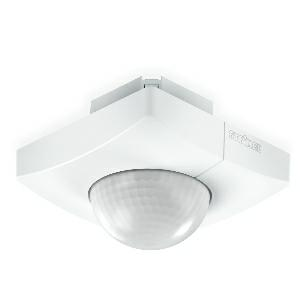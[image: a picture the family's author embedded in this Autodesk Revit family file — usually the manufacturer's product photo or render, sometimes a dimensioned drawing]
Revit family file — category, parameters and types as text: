
# Revit family: is_3360_033514
name_source: partatom
category: Elektroinstallationen
revit_build: Autodesk Revit 2016 (Build: 20190508_0715(x64)
units: mm (PartAtom-declared; Revit-internal decimal feet)

## family parameters
Basisbauteil = Fläche
Beim Laden mit Abzugskörper schneiden = Nein
Bemaßung runder Anschluss = Durchmesser verwenden
Beschriftungsausrichtung beibehalten = Nein
Gemeinsam genutzt = Nein
Raumberechnungspunkt = Nein
Teiletyp = Normal

## types (1)
- IS 3360
    Apparent Load = 0 VA
    Beschreibung = Type: Motion detectors; Dimensions (L x W x H): 78 x 94 x 94 mm; Mains power supply: 220 – 240 V / 50 – 60 Hz; Sensor Technology: passive infrared; Application, place: Indoors; Application, room: production facilities, recreation room, changing room, function room / ancillary room, sports hall, reception / lobby, stairwell, WC / washroom, multi-storey / underground car park, warehouse, Indoors; Installation site: ceiling; Installation: Concealed wiring; Switching zones: 1416 switching zones; Electronic scalability: No; Mechanical scalability: No; Mounting height: 2,50 – 4,00 m; Optimum mounting height: 2,8 m; Detection angle: 360 °; Angle of aperture: 180 °; Sneak-by guard: Yes; Capability of masking out individual segments: Yes; Reach, radial: Ø 8 m (50 m²); Reach, tangential: Ø 40 m (1257 m²); Reach, presence: Ø 3 m (7 m²); Twilight setting TEACH: Yes; Twilight setting: 2 – 1000 lx; Time setting: 5 sec – 15 min; Control output, Dali: Broadcast 1x30 electronic ballasts; Constant-lighting control: Yes; Basic light level function: Yes; Basic light level function in per cent: 10 – 50 %; Basic light level function time: 1-30 min, all night; Basic light level function percentage, from: 10 %; Basic light level function percentage, up to: 50 %; Functions: Normal / test mode, Manual ON / ON-OFF, Constant-lighting control ON-OFF; Settings via: Remote control, Potentiometers, Smart Remote; With remote control: No; Interconnection: Yes; IP-rating: IP20; Material: Plastic; Ambient temperature: -20 – 50 °C; Colour: white; Colour, RAL: 9003; Manufacturer's Warranty: 5 years; Version: DALI-2 Application Controller - concealed, sq.; PU1, EAN: 4007841033514
    Height = 0 mm  [stored 0 ft]
    Hersteller = Steinel
    Length = 78 mm  [stored 0.255906 ft]
    Maximum range = 20.158 m
    ModVariant = Nein
    Modell = 033514
    Mounting Place = Ceiling
    Mounting Type = Recessed
    Number of Poles = 1
    OnlyDefault = Ja
    Power Factor = 1
    Product Name = IS 3360
    Product group = Presence detector
    ProductGroupID = 4
    Protection Class = Protection class
    Protection Degree = IP 20
    RlxData = <blob elided: 159245 chars, md5=f7d2333f>
    Sensor characteristics = Circular 300°-360°
    Sensor type = Passive (infrared)
    SensorDataFile = <blob elided: 6785 chars, md5=23016e95>
    Type of entry = Presence, Motion
    Typenbild = produkt1_033514.jpg
    Typenkommentare = Product without accessories
    URL = http://relux.com
    VarID = ---
    Voltage = 0 V
    Vorgabe-Ansicht = 1800 mm
    Weight = 0.00 kg
    Width = 94 mm  [stored 0.308399 ft]

note: [stored X ft] marks values corroborated as IEEE doubles in the binary element streams (Revit-internal decimal feet)

## geometry (parser evidence)
native form markers: Blend x4, Sweep x13
no freeform markers — native parametric forms only
